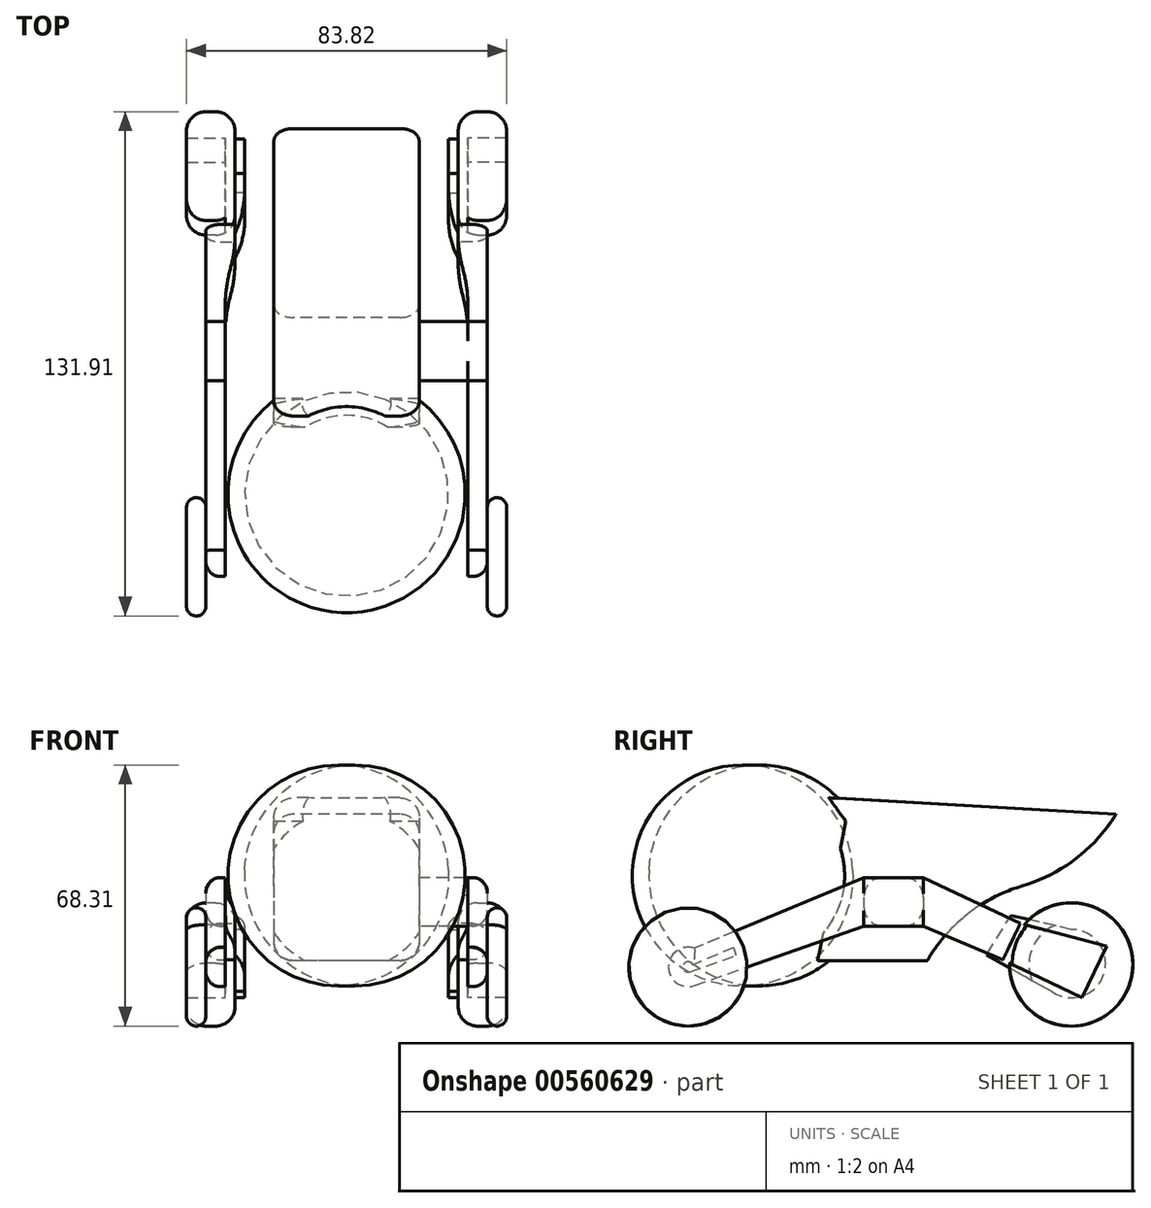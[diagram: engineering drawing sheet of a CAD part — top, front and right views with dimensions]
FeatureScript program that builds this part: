
annotation { "Feature Type Name" : "Feature", "Feature Type Description" : "" }
export const myFeature = defineFeature(function(context is Context, id is Id, definition is map)
    precondition{}
    {
        {
            var Q0;
            Q0=qCreatedBy(makeId("Right.planeOp"),FACE);
            var sketch = newSketch(context, id + "F0", { "sketchPlane" : qUnion([Q0])});
            skLineSegment(sketch, "E0", {"start": v(-40.88, 57.6) * mm, "end": v(-40.88, 0) * mm});
            skArc(sketch, "E1", {"start": v(-40.88, 57.6) * mm, "mid": v(-71.94, 28.8) * mm, "end": v(-40.88, 0) * mm});
            skSolve(sketch);
        }
        {
            var Q0;
            Q0=makeQuery(id+"F0.imprint","IMPRINT",FACE,{"disambiguationData":[TD([[makeQuery(id+"F0.imprint","IMPRINT",EDGE,{"derivedFrom":sQuery(id+"F0.wireOp",EDGE,"E0")}),-1.0]])]});
            var Q1;
            Q1=sQuery(id+"F0.wireOp",EDGE,"E0");
            revolve(context, id + "F1", {"entities" : qUnion([Q0]), "axis" : qUnion([Q1]), "revolveType" : RevolveType.FULL});
        }
        {
            var Q0;
            Q0=qCreatedBy(makeId("Right.planeOp"),FACE);
            var sketch = newSketch(context, id + "F2", { "sketchPlane" : qUnion([Q0])});
            skLineSegment(sketch, "E2", {"start": v(-16.01, 42.96) * mm, "end": v(-23.4, 6.52) * mm});
            skLineSegment(sketch, "E3", {"start": v(-23.4, 6.52) * mm, "end": v(54.7, 6.52) * mm});
            skLineSegment(sketch, "E4", {"start": v(54.7, 6.52) * mm, "end": v(54.7, 44.8) * mm});
            skLineSegment(sketch, "E5", {"start": v(54.7, 44.8) * mm, "end": v(-20.48, 49.1) * mm});
            skLineSegment(sketch, "E6", {"start": v(-20.48, 49.1) * mm, "end": v(-16.01, 42.96) * mm});
            skSolve(sketch);
        }
        {
            var Q0;
            Q0=makeQuery(id+"F2.imprint","IMPRINT",FACE,{"disambiguationData":[TD([[makeQuery(id+"F2.imprint","IMPRINT",EDGE,{"derivedFrom":sQuery(id+"F2.wireOp",EDGE,"E2")}),1.0]])]});
            extrude(context, id + "F3", {"entities" : qUnion([Q0]), "operationType" : NewBodyOperationType.ADD, "depth" : 19.05 * mm, "offsetDistance" : 25.4 * mm, "hasSecondDirection" : true, "secondDirectionOppositeDirection" : true, "secondDirectionDepth" : 19.05 * mm});
        }
        {
            var Q0;
            Q0=makeQuery(id+"F3.opExtrude","CAP_EDGE",EDGE,{"disambiguationData":[OSD([sQuery(id+"F2.wireOp",EDGE,"E5")])],"isStart":false});
            var Q1;
            Q1=makeQuery(id+"F3.opExtrude","CAP_EDGE",EDGE,{"disambiguationData":[OSD([sQuery(id+"F2.wireOp",EDGE,"E5")])],"isStart":true});
            var Q2;
            Q2=makeQuery(id+"F3.opExtrude","CAP_EDGE",EDGE,{"disambiguationData":[OSD([sQuery(id+"F2.wireOp",EDGE,"E3")])],"isStart":false});
            var Q3;
            Q3=makeQuery(id+"F3.opExtrude","CAP_EDGE",EDGE,{"disambiguationData":[OSD([sQuery(id+"F2.wireOp",EDGE,"E3")])],"isStart":true});
            fillet(context, id + "F4", {"entities" : qUnion([Q0, Q1, Q2, Q3]), "radius" : 5.08 * mm, "tangentPropagation" : true, "allowEdgeOverflow" : false});
        }
        {
            var Q0;
            Q0=qCreatedBy(makeId("Right.planeOp"),FACE);
            var sketch = newSketch(context, id + "F5", { "sketchPlane" : qUnion([Q0])});
            skLineSegment(sketch, "E7", {"start": v(13.06, 27.78) * mm, "end": v(58.85, 27.78) * mm});
            skLineSegment(sketch, "E8", {"start": v(58.85, 27.78) * mm, "end": v(58.85, 3.68) * mm});
            skLineSegment(sketch, "E9", {"start": v(58.85, 3.68) * mm, "end": v(4.26, 3.68) * mm});
            skLineSegment(sketch, "E10", {"start": v(4.26, 3.68) * mm, "end": v(13.06, 27.78) * mm});
            skSolve(sketch);
        }
        {
            var Q0;
            Q0=makeQuery(id+"F5.imprint","IMPRINT",FACE,{"disambiguationData":[TD([[makeQuery(id+"F5.imprint","IMPRINT",EDGE,{"derivedFrom":sQuery(id+"F5.wireOp",EDGE,"E7")}),-1.0]])]});
            extrude(context, id + "F6", {"entities" : qUnion([Q0]), "operationType" : NewBodyOperationType.REMOVE, "oppositeDirection" : true, "depth" : 25.4 * mm, "offsetDistance" : 25.4 * mm, "hasSecondDirection" : true, "secondDirectionOppositeDirection" : false, "secondDirectionDepth" : 25.4 * mm});
        }
        {
            var Q0;
            Q0=makeQuery(id+"F3.opExtrude","CAP_FACE",FACE,{"disambiguationData":[OSD([sQuery(id+"F2.wireOp",EDGE,"E2"),sQuery(id+"F2.wireOp",EDGE,"E3"),sQuery(id+"F2.wireOp",EDGE,"E4"),sQuery(id+"F2.wireOp",EDGE,"E5"),sQuery(id+"F2.wireOp",EDGE,"E6")])],"isStart":false});
            var sketch = newSketch(context, id + "F7", { "sketchPlane" : qUnion([Q0])});
            skLineSegment(sketch, "E11.bottom", {"start": v(-11.31, 28.24) * mm, "end": v(4.28, 28.24) * mm});
            skLineSegment(sketch, "E11.top", {"start": v(-11.31, 15.54) * mm, "end": v(4.28, 15.54) * mm});
            skLineSegment(sketch, "E11.left", {"start": v(-11.31, 28.24) * mm, "end": v(-11.31, 15.54) * mm});
            skLineSegment(sketch, "E11.right", {"start": v(4.28, 28.24) * mm, "end": v(4.28, 15.54) * mm});
            skSolve(sketch);
        }
        {
            var Q0;
            Q0=makeQuery(id+"F7.imprint","IMPRINT",FACE,{"disambiguationData":[TD([[makeQuery(id+"F7.imprint","IMPRINT",EDGE,{"derivedFrom":sQuery(id+"F7.wireOp",EDGE,"E11.bottom")}),-1.0]])]});
            extrude(context, id + "F8", {"entities" : qUnion([Q0]), "operationType" : NewBodyOperationType.ADD, "depth" : 12.7 * mm, "offsetDistance" : 25.4 * mm});
        }
        {
            var Q0;
            Q0=makeQuery(id+"F8.opExtrude","CAP_FACE",FACE,{"disambiguationData":[OSD([sQuery(id+"F7.wireOp",EDGE,"E11.bottom"),sQuery(id+"F7.wireOp",EDGE,"E11.top"),sQuery(id+"F7.wireOp",EDGE,"E11.left"),sQuery(id+"F7.wireOp",EDGE,"E11.right")])],"isStart":false});
            var sketch = newSketch(context, id + "F9", { "sketchPlane" : qUnion([Q0])});
            skLineSegment(sketch, "E12", {"start": v(-11.31, 28.24) * mm, "end": v(-55.63, 9.72) * mm});
            skLineSegment(sketch, "E13", {"start": v(-55.63, 9.72) * mm, "end": v(-55.63, 0) * mm});
            skLineSegment(sketch, "E14", {"start": v(-55.63, 0) * mm, "end": v(-11.31, 15.54) * mm});
            skLineSegment(sketch, "E15", {"start": v(-11.31, 15.54) * mm, "end": v(-11.31, 28.24) * mm});
            skArc(sketch, "E16", {"start": v(-55.63, 9.72) * mm, "mid": v(-62.48, 4.86) * mm, "end": v(-55.63, 0) * mm});
            skSolve(sketch);
        }
        {
            var Q0;
            Q0=makeQuery(id+"F9.imprint","IMPRINT",FACE,{"disambiguationData":[TD([[makeQuery(id+"F9.imprint","IMPRINT",EDGE,{"derivedFrom":sQuery(id+"F9.wireOp",EDGE,"E12")}),1.0]])]});
            var Q1;
            Q1=makeQuery(id+"F9.imprint","IMPRINT",FACE,{"disambiguationData":[TD([[makeQuery(id+"F9.imprint","IMPRINT",EDGE,{"derivedFrom":sQuery(id+"F9.wireOp",EDGE,"E13")}),-1.0]])]});
            extrude(context, id + "F10", {"entities" : qUnion([Q0, Q1]), "depth" : 5.08 * mm, "offsetDistance" : 25.4 * mm});
        }
        {
            var Q0;
            Q0=makeQuery(id+"F10.opExtrude","SWEPT_FACE",FACE,{"disambiguationData":[OSD([sQuery(id+"F9.wireOp",EDGE,"E15")])]});
            extrude(context, id + "F11", {"entities" : qUnion([Q0]), "depth" : 10.16 * mm, "offsetDistance" : 25.4 * mm});
        }
        {
            var Q0;
            Q0=makeQuery(id+"F8.opExtrude","CAP_FACE",FACE,{"disambiguationData":[OSD([sQuery(id+"F7.wireOp",EDGE,"E11.bottom"),sQuery(id+"F7.wireOp",EDGE,"E11.top"),sQuery(id+"F7.wireOp",EDGE,"E11.left"),sQuery(id+"F7.wireOp",EDGE,"E11.right")])],"isStart":false});
            var sketch = newSketch(context, id + "F12", { "sketchPlane" : qUnion([Q0])});
            skLineSegment(sketch, "E17", {"start": v(4.28, 28.24) * mm, "end": v(40.76, 10.9) * mm});
            skLineSegment(sketch, "E18", {"start": v(40.76, 10.9) * mm, "end": v(40.76, 0) * mm});
            skLineSegment(sketch, "E19", {"start": v(40.76, 0) * mm, "end": v(4.28, 15.54) * mm});
            skLineSegment(sketch, "E20", {"start": v(4.28, 15.54) * mm, "end": v(4.28, 28.24) * mm});
            skArc(sketch, "E21", {"start": v(40.76, 0) * mm, "mid": v(49, 5.45) * mm, "end": v(40.76, 10.9) * mm});
            skSolve(sketch);
        }
        {
            var Q0;
            Q0=makeQuery(id+"F12.imprint","IMPRINT",FACE,{"disambiguationData":[TD([[makeQuery(id+"F12.imprint","IMPRINT",EDGE,{"derivedFrom":sQuery(id+"F12.wireOp",EDGE,"E17")}),-1.0]])]});
            var Q1;
            Q1=makeQuery(id+"F12.imprint","IMPRINT",FACE,{"disambiguationData":[TD([[makeQuery(id+"F12.imprint","IMPRINT",EDGE,{"derivedFrom":sQuery(id+"F12.wireOp",EDGE,"E18")}),1.0]])]});
            extrude(context, id + "F13", {"entities" : qUnion([Q0, Q1]), "depth" : 5.08 * mm, "offsetDistance" : 25.4 * mm});
        }
        {
            var Q0;
            Q0=makeQuery(id+"F13.opExtrude","SWEPT_FACE",FACE,{"disambiguationData":[OSD([sQuery(id+"F12.wireOp",EDGE,"E20")])]});
            extrude(context, id + "F14", {"entities" : qUnion([Q0]), "depth" : 3.8 * mm, "offsetDistance" : 25.4 * mm});
        }
        {
            var Q0;
            Q0=makeQuery(id+"F14.opExtrude","CAP_FACE",FACE,{"disambiguationData":[OSD([sQuery(id+"F12.wireOp",EDGE,"E20")])],"isStart":false});
            extrude(context, id + "F15", {"entities" : qUnion([Q0]), "depth" : 5.08 * mm, "offsetDistance" : 25.4 * mm});
        }
        {
            var Q0;
            {var subQ0=sQuery(id+"F12.wireOp",EDGE,"E20");var subQ1=sQuery(id+"F12.wireOp",EDGE,"E17");var subQ2=sQuery(id+"F7.wireOp",EDGE,"E11.bottom");Q0=makeQuery(id+"F14.opExtrude","SWEPT_EDGE",EDGE,{"disambiguationData":[OSD([subQ2,subQ1,subQ0]),TDD([makeQuery(id+"F13.opExtrude","CAP_VERTEX",VERTEX,{"disambiguationData":[OSD([subQ2,subQ1,subQ0])],"isStart":false})])]});}
            var Q1;
            {var subQ0=sQuery(id+"F12.wireOp",EDGE,"E20");var subQ1=sQuery(id+"F12.wireOp",EDGE,"E17");var subQ2=sQuery(id+"F7.wireOp",EDGE,"E11.bottom");Q1=makeQuery(id+"F15.opExtrude","SWEPT_EDGE",EDGE,{"disambiguationData":[OSD([subQ2,subQ1,subQ0]),TDD([makeQuery(id+"F14.opExtrude","CAP_VERTEX",VERTEX,{"disambiguationData":[OSD([subQ2,subQ1,subQ0]),TDD([makeQuery(id+"F13.opExtrude","CAP_VERTEX",VERTEX,{"disambiguationData":[OSD([subQ2,subQ1,subQ0])],"isStart":false})])],"isStart":false})])]});}
            var Q2;
            {var subQ0=sQuery(id+"F9.wireOp",EDGE,"E15");var subQ1=sQuery(id+"F9.wireOp",EDGE,"E12");var subQ2=sQuery(id+"F7.wireOp",EDGE,"E11.bottom");Q2=makeQuery(id+"F11.opExtrude","SWEPT_EDGE",EDGE,{"disambiguationData":[OSD([subQ2,subQ1,subQ0]),TDD([makeQuery(id+"F10.opExtrude","CAP_VERTEX",VERTEX,{"disambiguationData":[OSD([subQ2,subQ1,subQ0])],"isStart":false})])]});}
            var Q3;
            Q3=makeQuery(id+"F13.opExtrude","CAP_EDGE",EDGE,{"disambiguationData":[OSD([sQuery(id+"F12.wireOp",EDGE,"E17")])],"isStart":false});
            var Q4;
            Q4=makeQuery(id+"F10.opExtrude","CAP_EDGE",EDGE,{"disambiguationData":[OSD([sQuery(id+"F9.wireOp",EDGE,"E12")])],"isStart":false});
            var Q5;
            Q5=makeQuery(id+"F10.opExtrude","CAP_EDGE",EDGE,{"disambiguationData":[OSD([sQuery(id+"F9.wireOp",EDGE,"E14")])],"isStart":false});
            var Q6;
            Q6=makeQuery(id+"F13.opExtrude","CAP_EDGE",EDGE,{"disambiguationData":[OSD([sQuery(id+"F12.wireOp",EDGE,"E19")])],"isStart":false});
            var Q7;
            {var subQ0=sQuery(id+"F9.wireOp",EDGE,"E15");var subQ1=sQuery(id+"F9.wireOp",EDGE,"E14");var subQ2=sQuery(id+"F7.wireOp",EDGE,"E11.top");Q7=makeQuery(id+"F11.opExtrude","SWEPT_EDGE",EDGE,{"disambiguationData":[OSD([subQ2,subQ1,subQ0]),TDD([makeQuery(id+"F10.opExtrude","CAP_VERTEX",VERTEX,{"disambiguationData":[OSD([subQ2,subQ1,subQ0])],"isStart":false})])]});}
            var Q8;
            {var subQ0=sQuery(id+"F12.wireOp",EDGE,"E20");var subQ1=sQuery(id+"F12.wireOp",EDGE,"E19");var subQ2=sQuery(id+"F7.wireOp",EDGE,"E11.top");Q8=makeQuery(id+"F14.opExtrude","SWEPT_EDGE",EDGE,{"disambiguationData":[OSD([subQ2,subQ1,subQ0]),TDD([makeQuery(id+"F13.opExtrude","CAP_VERTEX",VERTEX,{"disambiguationData":[OSD([subQ2,subQ1,subQ0])],"isStart":false})])]});}
            var Q9;
            {var subQ0=sQuery(id+"F12.wireOp",EDGE,"E20");var subQ1=sQuery(id+"F12.wireOp",EDGE,"E19");var subQ2=sQuery(id+"F7.wireOp",EDGE,"E11.top");Q9=makeQuery(id+"F15.opExtrude","SWEPT_EDGE",EDGE,{"disambiguationData":[OSD([subQ2,subQ1,subQ0]),TDD([makeQuery(id+"F14.opExtrude","CAP_VERTEX",VERTEX,{"disambiguationData":[OSD([subQ2,subQ1,subQ0]),TDD([makeQuery(id+"F13.opExtrude","CAP_VERTEX",VERTEX,{"disambiguationData":[OSD([subQ2,subQ1,subQ0])],"isStart":false})])],"isStart":false})])]});}
            fillet(context, id + "F16", {"entities" : qUnion([Q0, Q1, Q2, Q3, Q4, Q5, Q6, Q7, Q8, Q9]), "radius" : 3.8 * mm, "tangentPropagation" : true, "allowEdgeOverflow" : false});
        }
        {
            var Q0;
            Q0=makeQuery(id+"F10.opExtrude","CAP_FACE",FACE,{"disambiguationData":[OSD([sQuery(id+"F9.wireOp",EDGE,"E12"),sQuery(id+"F9.wireOp",EDGE,"E14"),sQuery(id+"F9.wireOp",EDGE,"E15"),sQuery(id+"F9.wireOp",EDGE,"E16")])],"isStart":false});
            var sketch = newSketch(context, id + "F17", { "sketchPlane" : qUnion([Q0])});
            skLineSegment(sketch, "E22", {"start": v(-76.65, -10.62) * mm, "end": v(65.15, -10.62) * mm});
            skCircle(sketch, "E23", {"center": v(-57.33, 4.86) * mm, "radius": 15.48 * mm});
            skCircle(sketch, "E24", {"center": v(42.97, 5.5) * mm, "radius": 16.13 * mm});
            skSolve(sketch);
        }
        {
            var Q0;
            {var subQ0=sQuery(id+"F9.wireOp",EDGE,"E16");var subQ1=sQuery(id+"F9.wireOp",EDGE,"E14");var subQ2=sQuery(id+"F9.wireOp",EDGE,"E12");var subQ3=makeQuery(id+"F10.opExtrude","CAP_FACE",FACE,{"disambiguationData":[OSD([subQ2,subQ1,sQuery(id+"F9.wireOp",EDGE,"E15"),subQ0])],"isStart":false});var subQ4=makeQuery(id+"F16.opFillet","BLEND_EDGE",EDGE,{"blendedFrom":[makeQuery(id+"F10.opExtrude","CAP_EDGE",EDGE,{"disambiguationData":[OSD([subQ0])],"isStart":false}),subQ3],"blendedInto":[subQ3]});Q0=makeQuery(id+"F17.imprint","IMPRINT",FACE,{"disambiguationData":[TD([[makeQuery(id+"F17.imprint","IMPRINT",EDGE,{"derivedFrom":subQ4}),-1.0]])]});}
            var Q1;
            {var subQ1=sQuery(id+"F9.wireOp",EDGE,"E16");var subQ2=sQuery(id+"F9.wireOp",EDGE,"E14");var subQ3=sQuery(id+"F9.wireOp",EDGE,"E12");var subQ4=makeQuery(id+"F10.opExtrude","CAP_FACE",FACE,{"disambiguationData":[OSD([subQ3,subQ2,sQuery(id+"F9.wireOp",EDGE,"E15"),subQ1])],"isStart":false});var subQ9=makeQuery(id+"F16.opFillet","BLEND_EDGE",EDGE,{"blendedFrom":[makeQuery(id+"F10.opExtrude","CAP_EDGE",EDGE,{"disambiguationData":[OSD([subQ1])],"isStart":false}),subQ4],"blendedInto":[subQ4]});Q1=makeQuery(id+"F17.imprint","IMPRINT",FACE,{"disambiguationData":[TD([[makeQuery(id+"F17.imprint","IMPRINT",EDGE,{"derivedFrom":subQ9}),1.0]])]});}
            var Q2;
            Q2=makeQuery(id+"F17.imprint","IMPRINT",FACE,{"disambiguationData":[TD([[makeQuery(id+"F17.imprint","IMPRINT",EDGE,{"derivedFrom":sQuery(id+"F17.wireOp",EDGE,"E24")}),1.0]])]});
            extrude(context, id + "F18", {"entities" : qUnion([Q0, Q1, Q2]), "depth" : 5.08 * mm, "offsetDistance" : 25.4 * mm});
        }
        {
            var Q0;
            Q0=makeQuery(id+"F18.opExtrude","CAP_FACE",FACE,{"disambiguationData":[OSD([sQuery(id+"F17.wireOp",EDGE,"E24")])],"isStart":true});
            extrude(context, id + "F19", {"entities" : qUnion([Q0]), "depth" : 7.62 * mm, "offsetDistance" : 25.4 * mm});
        }
        {
            var Q0;
            Q0=makeQuery(id+"F18.opExtrude","CAP_EDGE",EDGE,{"disambiguationData":[OSD([sQuery(id+"F17.wireOp",EDGE,"E23")])],"isStart":false});
            var Q1;
            Q1=makeQuery(id+"F18.opExtrude","CAP_EDGE",EDGE,{"disambiguationData":[OSD([sQuery(id+"F17.wireOp",EDGE,"E23")])],"isStart":true});
            fillet(context, id + "F20", {"entities" : qUnion([Q0, Q1]), "radius" : 2.54 * mm, "tangentPropagation" : true, "allowEdgeOverflow" : false});
        }
        {
            var Q0;
            Q0=makeQuery(id+"F18.opExtrude","CAP_EDGE",EDGE,{"disambiguationData":[OSD([sQuery(id+"F17.wireOp",EDGE,"E24")])],"isStart":false});
            var Q1;
            Q1=makeQuery(id+"F19.opExtrude","CAP_EDGE",EDGE,{"disambiguationData":[OSD([sQuery(id+"F17.wireOp",EDGE,"E24")])],"isStart":false});
            fillet(context, id + "F21", {"entities" : qUnion([Q0, Q1]), "radius" : 5.08 * mm, "tangentPropagation" : true, "allowEdgeOverflow" : false});
        }
        {
            var Q0;
            Q0=makeQuery(id+"F13.opExtrude","CAP_FACE",FACE,{"disambiguationData":[OSD([sQuery(id+"F12.wireOp",EDGE,"E17"),sQuery(id+"F12.wireOp",EDGE,"E19"),sQuery(id+"F12.wireOp",EDGE,"E20"),sQuery(id+"F12.wireOp",EDGE,"E21")])],"isStart":true});
            var sketch = newSketch(context, id + "F22", { "sketchPlane" : qUnion([Q0])});
            skLineSegment(sketch, "E25", {"start": v(-29.6, 16.2) * mm, "end": v(-25.08, 6.68) * mm});
            skLineSegment(sketch, "E26", {"start": v(-25.08, 6.68) * mm, "end": v(-45.84, -3.19) * mm});
            skLineSegment(sketch, "E27", {"start": v(-45.84, -3.19) * mm, "end": v(-52.24, 10.3) * mm});
            skLineSegment(sketch, "E28", {"start": v(-52.24, 10.3) * mm, "end": v(-29.6, 16.2) * mm});
            skSolve(sketch);
        }
        {
            var Q0;
            {var subQ0=sQuery(id+"F22.wireOp",EDGE,"E25");Q0=makeQuery(id+"F22.imprint","IMPRINT",FACE,{"disambiguationData":[TD([[makeQuery(id+"F22.imprint","IMPRINT",EDGE,{"derivedFrom":subQ0}),-1.0]])]});}
            var Q1;
            {var subQ2=sQuery(id+"F22.wireOp",EDGE,"E26");Q1=makeQuery(id+"F22.imprint","IMPRINT",FACE,{"disambiguationData":[TD([[makeQuery(id+"F22.imprint","IMPRINT",EDGE,{"derivedFrom":subQ2}),-1.0]])]});}
            extrude(context, id + "F23", {"entities" : qUnion([Q0, Q1]), "operationType" : NewBodyOperationType.REMOVE, "oppositeDirection" : true, "depth" : 25.4 * mm, "offsetDistance" : 25.4 * mm});
        }
        {
            var Q0;
            Q0=makeQuery(id+"F13.opExtrude","CAP_FACE",FACE,{"disambiguationData":[OSD([sQuery(id+"F12.wireOp",EDGE,"E17"),sQuery(id+"F12.wireOp",EDGE,"E19"),sQuery(id+"F12.wireOp",EDGE,"E20"),sQuery(id+"F12.wireOp",EDGE,"E21")])],"isStart":true});
            var sketch = newSketch(context, id + "F24", { "sketchPlane" : qUnion([Q0])});
            skLineSegment(sketch, "E29", {"start": v(-29.6, 16.2) * mm, "end": v(-25.08, 6.68) * mm});
            skLineSegment(sketch, "E30", {"start": v(-25.08, 6.68) * mm, "end": v(-9.81, 13.18) * mm});
            skLineSegment(sketch, "E31", {"start": v(-9.81, 13.18) * mm, "end": v(-16.95, 22.22) * mm});
            skLineSegment(sketch, "E32", {"start": v(-16.95, 22.22) * mm, "end": v(-29.6, 16.2) * mm});
            skSolve(sketch);
        }
        {
            var Q0;
            Q0=makeQuery(id+"F24.imprint","IMPRINT",FACE,{"disambiguationData":[TD([[makeQuery(id+"F24.imprint","IMPRINT",EDGE,{"derivedFrom":sQuery(id+"F24.wireOp",EDGE,"E29")}),1.0]])]});
            extrude(context, id + "F25", {"entities" : qUnion([Q0]), "operationType" : NewBodyOperationType.ADD, "depth" : 2.54 * mm, "offsetDistance" : 25.4 * mm});
        }
        {
            var Q0;
            Q0=makeQuery(id+"F25.opExtrude","CAP_FACE",FACE,{"disambiguationData":[OSD([sQuery(id+"F24.wireOp",EDGE,"E29"),sQuery(id+"F24.wireOp",EDGE,"E30"),sQuery(id+"F24.wireOp",EDGE,"E31"),sQuery(id+"F24.wireOp",EDGE,"E32")])],"isStart":false});
            var sketch = newSketch(context, id + "F26", { "sketchPlane" : qUnion([Q0])});
            skCircle(sketch, "E33", {"center": v(-43.03, 5.73) * mm, "radius": 8.93 * mm});
            skLineSegment(sketch, "E34", {"start": v(-43.03, 14.67) * mm, "end": v(-23.28, 19.22) * mm});
            skLineSegment(sketch, "E35", {"start": v(-23.28, 19.22) * mm, "end": v(-17.45, 9.93) * mm});
            skLineSegment(sketch, "E36", {"start": v(-17.45, 9.93) * mm, "end": v(-37.88, -1.57) * mm});
            skSolve(sketch);
        }
        {
            var Q0;
            Q0 = qSketchRegion(id + "FPhgOQThtUDPnLO_9", true);
            var Q1;
            {var subQ0=sQuery(id+"F26.wireOp",EDGE,"E35");Q1=makeQuery(id+"F26.imprint","IMPRINT",FACE,{"disambiguationData":[TD([[makeQuery(id+"F26.imprint","IMPRINT",EDGE,{"derivedFrom":subQ0}),-1.0]])]});}
            var Q2;
            {var subQ2=sQuery(id+"F26.wireOp",EDGE,"E34");Q2=makeQuery(id+"F26.imprint","IMPRINT",FACE,{"disambiguationData":[TD([[makeQuery(id+"F26.imprint","IMPRINT",EDGE,{"derivedFrom":subQ2}),-1.0]])]});}
            var Q3;
            {var subQ0=sQuery(id+"F26.wireOp",EDGE,"E33");var subQ1=makeQuery(id+"F26.imprint","INTERSECT",VERTEX,{"derivedFrom":[subQ0,sQuery(id+"F26.wireOp",EDGE,"E34")]});Q3=makeQuery(id+"F26.imprint","IMPRINT",FACE,{"disambiguationData":[TD([[makeQuery(id+"F26.imprint","IMPRINT",EDGE,{"disambiguationData":[TD([[subQ1,-1.0]])],"derivedFrom":subQ0}),1.0]])]});}
            extrude(context, id + "F27", {"entities" : qUnion([Q0, Q1, Q2, Q3]), "depth" : 2.54 * mm, "offsetDistance" : 25.4 * mm});
        }
        {
            var Q0;
            Q0=makeQuery(id+"F27.opExtrude","CAP_EDGE",EDGE,{"disambiguationData":[OSD([sQuery(id+"F26.wireOp",EDGE,"E35")])],"isStart":false});
            chamfer(context, id + "F28", {"entities" : qUnion([Q0]), "chamferType" : ChamferType.TWO_OFFSETS, "width1" : 5.08 * mm, "oppositeDirection" : false, "width2" : 7.62 * mm, "tangentPropagation" : true});
        }
        {
            var Q0;
            Q0=makeQuery(id+"F25.opExtrude","CAP_EDGE",EDGE,{"disambiguationData":[OSD([sQuery(id+"F24.wireOp",EDGE,"E31")])],"isStart":false});
            chamfer(context, id + "F29", {"entities" : qUnion([Q0]), "width" : 5.08 * mm, "tangentPropagation" : true});
        }
        {
            var Q0;
            Q0=makeQuery(id+"F29.opChamfer","BLEND_EDGE",EDGE,{"blendedFrom":[makeQuery(id+"F25.opExtrude","CAP_EDGE",EDGE,{"disambiguationData":[OSD([sQuery(id+"F24.wireOp",EDGE,"E31")])],"isStart":false}),makeQuery(id+"F13.opExtrude","CAP_FACE",FACE,{"disambiguationData":[OSD([sQuery(id+"F12.wireOp",EDGE,"E17"),sQuery(id+"F12.wireOp",EDGE,"E19"),sQuery(id+"F12.wireOp",EDGE,"E20"),sQuery(id+"F12.wireOp",EDGE,"E21")])],"isStart":true})],"blendedInto":[makeQuery(id+"F13.opExtrude","CAP_FACE",FACE,{"disambiguationData":[OSD([sQuery(id+"F12.wireOp",EDGE,"E17"),sQuery(id+"F12.wireOp",EDGE,"E19"),sQuery(id+"F12.wireOp",EDGE,"E20"),sQuery(id+"F12.wireOp",EDGE,"E21")])],"isStart":true})]});
            fillet(context, id + "F30", {"entities" : qUnion([Q0]), "radius" : 42.1 * mm, "tangentPropagation" : true, "allowEdgeOverflow" : false});
        }
        {
            var Q0;
            {var subQ0=sQuery(id+"F24.wireOp",EDGE,"E31");Q0=makeQuery(id+"F30.opFillet","BLEND_EDGE",EDGE,{"blendedFrom":[makeQuery(id+"F29.opChamfer","BLEND_EDGE",EDGE,{"blendedFrom":[makeQuery(id+"F25.opExtrude","CAP_EDGE",EDGE,{"disambiguationData":[OSD([subQ0])],"isStart":false}),makeQuery(id+"F13.opExtrude","CAP_FACE",FACE,{"disambiguationData":[OSD([sQuery(id+"F12.wireOp",EDGE,"E17"),sQuery(id+"F12.wireOp",EDGE,"E19"),sQuery(id+"F12.wireOp",EDGE,"E20"),sQuery(id+"F12.wireOp",EDGE,"E21")])],"isStart":true})],"blendedInto":[makeQuery(id+"F13.opExtrude","CAP_FACE",FACE,{"disambiguationData":[OSD([sQuery(id+"F12.wireOp",EDGE,"E17"),sQuery(id+"F12.wireOp",EDGE,"E19"),sQuery(id+"F12.wireOp",EDGE,"E20"),sQuery(id+"F12.wireOp",EDGE,"E21")])],"isStart":true})]}),makeQuery(id+"F25.opExtrude","CAP_FACE",FACE,{"disambiguationData":[OSD([sQuery(id+"F24.wireOp",EDGE,"E29"),sQuery(id+"F24.wireOp",EDGE,"E30"),subQ0,sQuery(id+"F24.wireOp",EDGE,"E32")])],"isStart":false})],"blendedInto":[makeQuery(id+"F25.opExtrude","CAP_FACE",FACE,{"disambiguationData":[OSD([sQuery(id+"F24.wireOp",EDGE,"E29"),sQuery(id+"F24.wireOp",EDGE,"E30"),subQ0,sQuery(id+"F24.wireOp",EDGE,"E32")])],"isStart":false})]});}
            fillet(context, id + "F31", {"entities" : qUnion([Q0]), "radius" : 37.3 * mm, "tangentPropagation" : true, "allowEdgeOverflow" : false});
        }
        {
            var Q0;
            {var subQ0=sQuery(id+"F26.wireOp",EDGE,"E35");Q0=makeQuery(id+"F28.opChamfer","BLEND_EDGE",EDGE,{"blendedFrom":[makeQuery(id+"F27.opExtrude","CAP_EDGE",EDGE,{"disambiguationData":[OSD([subQ0])],"isStart":false}),makeQuery(id+"F27.opExtrude","CAP_FACE",FACE,{"disambiguationData":[OSD([sQuery(id+"F26.wireOp",EDGE,"E33"),sQuery(id+"F26.wireOp",EDGE,"E34"),subQ0,sQuery(id+"F26.wireOp",EDGE,"E36")])],"isStart":false})],"blendedInto":[makeQuery(id+"F27.opExtrude","CAP_FACE",FACE,{"disambiguationData":[OSD([sQuery(id+"F26.wireOp",EDGE,"E33"),sQuery(id+"F26.wireOp",EDGE,"E34"),subQ0,sQuery(id+"F26.wireOp",EDGE,"E36")])],"isStart":false})]});}
            fillet(context, id + "F32", {"entities" : qUnion([Q0]), "radius" : 27.32 * mm, "tangentPropagation" : true, "allowEdgeOverflow" : false});
        }
        {
            var Q0;
            Q0=makeQuery(id+"F8.opExtrude","SWEPT_EDGE",EDGE,{"disambiguationData":[OSD([sQuery(id+"F7.wireOp",EDGE,"E11.bottom"),sQuery(id+"F7.wireOp",EDGE,"E11.left")])]});
            var Q1;
            Q1=makeQuery(id+"F8.opExtrude","SWEPT_EDGE",EDGE,{"disambiguationData":[OSD([sQuery(id+"F7.wireOp",EDGE,"E11.bottom"),sQuery(id+"F7.wireOp",EDGE,"E11.right")])]});
            var Q2;
            Q2=makeQuery(id+"F8.opExtrude","SWEPT_EDGE",EDGE,{"disambiguationData":[OSD([sQuery(id+"F7.wireOp",EDGE,"E11.top"),sQuery(id+"F7.wireOp",EDGE,"E11.left")])]});
            var Q3;
            Q3=makeQuery(id+"F8.opExtrude","SWEPT_EDGE",EDGE,{"disambiguationData":[OSD([sQuery(id+"F7.wireOp",EDGE,"E11.top"),sQuery(id+"F7.wireOp",EDGE,"E11.right")])]});
            fillet(context, id + "F33", {"entities" : qUnion([Q0, Q1, Q2, Q3]), "radius" : 5.08 * mm, "tangentPropagation" : true, "allowEdgeOverflow" : false});
        }
        {
            var Q0;
            Q0=makeQuery(id+"F18.opExtrude","SWEPT_BODY",BODY,{"disambiguationData":[OSD([sQuery(id+"F17.wireOp",EDGE,"E23")])]});
            var Q1;
            Q1=makeQuery(id+"F10.opExtrude","SWEPT_BODY",BODY,{"disambiguationData":[OSD([sQuery(id+"F9.wireOp",EDGE,"E12"),sQuery(id+"F9.wireOp",EDGE,"E14"),sQuery(id+"F9.wireOp",EDGE,"E15"),sQuery(id+"F9.wireOp",EDGE,"E16")])]});
            var Q2;
            Q2=makeQuery(id+"F15.opExtrude","SWEPT_BODY",BODY,{"disambiguationData":[OSD([sQuery(id+"F12.wireOp",EDGE,"E20")])]});
            var Q3;
            Q3=makeQuery(id+"F14.opExtrude","SWEPT_BODY",BODY,{"disambiguationData":[OSD([sQuery(id+"F12.wireOp",EDGE,"E20")])]});
            var Q4;
            Q4=makeQuery(id+"F13.opExtrude","SWEPT_BODY",BODY,{"disambiguationData":[OSD([sQuery(id+"F12.wireOp",EDGE,"E17"),sQuery(id+"F12.wireOp",EDGE,"E19"),sQuery(id+"F12.wireOp",EDGE,"E20"),sQuery(id+"F12.wireOp",EDGE,"E21")])]});
            var Q5;
            Q5=makeQuery(id+"F27.opExtrude","SWEPT_BODY",BODY,{"disambiguationData":[OSD([sQuery(id+"F26.wireOp",EDGE,"E33"),sQuery(id+"F26.wireOp",EDGE,"E34"),sQuery(id+"F26.wireOp",EDGE,"E35"),sQuery(id+"F26.wireOp",EDGE,"E36")])]});
            var Q6;
            Q6=makeQuery(id+"F18.opExtrude","SWEPT_BODY",BODY,{"disambiguationData":[OSD([sQuery(id+"F17.wireOp",EDGE,"E24")])]});
            var Q7;
            Q7=makeQuery(id+"F19.opExtrude","SWEPT_BODY",BODY,{"disambiguationData":[OSD([sQuery(id+"F17.wireOp",EDGE,"E24")])]});
            var Q8;
            Q8=makeQuery(id+"F11.opExtrude","SWEPT_BODY",BODY,{"disambiguationData":[OSD([sQuery(id+"F9.wireOp",EDGE,"E15")])]});
            var Q9;
            Q9=qCreatedBy(makeId("Right.planeOp"),FACE);
            mirror(context, id + "F34", {"operationType" : NewBodyOperationType.ADD, "entities" : qUnion([Q0, Q1, Q2, Q3, Q4, Q5, Q6, Q7, Q8]), "mirrorPlane" : qUnion([Q9])});
        }
        {
            var Q0;
            Q0=makeQuery(id+"F6.boolean.opBoolean","COPY",EDGE,{"derivedFrom":makeQuery(id+"F6.opExtrude","SWEPT_EDGE",EDGE,{"disambiguationData":[OSD([sQuery(id+"F5.wireOp",EDGE,"E7"),sQuery(id+"F5.wireOp",EDGE,"E10")])]})});
            fillet(context, id + "F35", {"entities" : qUnion([Q0]), "radius" : 42.72 * mm, "tangentPropagation" : true, "allowEdgeOverflow" : false});
        }
        {
            var Q0;
            Q0=makeQuery(id+"F6.boolean.opBoolean","INTERSECT",EDGE,{"derivedFrom":[makeQuery(id+"F3.opExtrude","SWEPT_FACE",FACE,{"disambiguationData":[OSD([sQuery(id+"F2.wireOp",EDGE,"E4")])]}),makeQuery(id+"F6.opExtrude","SWEPT_FACE",FACE,{"disambiguationData":[OSD([sQuery(id+"F5.wireOp",EDGE,"E7")])]})]});
            fillet(context, id + "F36", {"entities" : qUnion([Q0]), "radius" : 43.5 * mm, "tangentPropagation" : true, "allowEdgeOverflow" : false});
        }
    });
